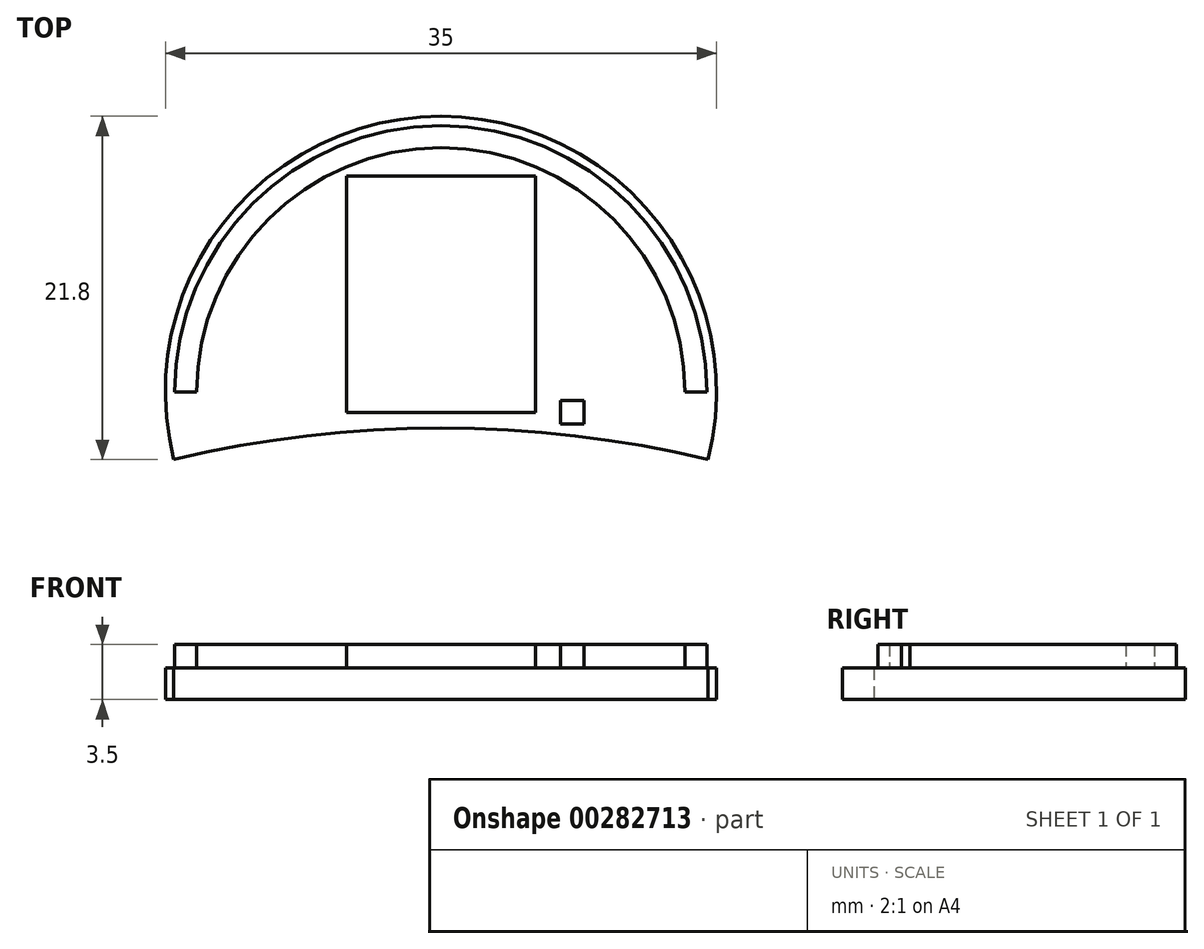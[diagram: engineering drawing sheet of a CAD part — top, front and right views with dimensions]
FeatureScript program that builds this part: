
annotation { "Feature Type Name" : "Feature", "Feature Type Description" : "" }
export const myFeature = defineFeature(function(context is Context, id is Id, definition is map)
    precondition{}
    {
        {
            var Q0;
            Q0=qCreatedBy(makeId("Top.planeOp"),FACE);
            var sketch = newSketch(context, id + "F0", { "sketchPlane" : qUnion([Q0])});
            skCircle(sketch, "E0", {"center": v(0, 0) * mm, "radius": 17.5 * mm});
            skArc(sketch, "E1", {"start": v(16.96, -4.3) * mm, "mid": v(0, -2.3) * mm, "end": v(-16.96, -4.3) * mm});
            skLineSegment(sketch, "E2", {"start": v(16.96, -4.3) * mm, "end": v(-16.96, -4.3) * mm, "construction": true});
            skLineSegment(sketch, "E3", {"start": v(0, -2.3) * mm, "end": v(0, -4.3) * mm, "construction": true});
            skLineSegment(sketch, "E4", {"start": v(0, 17.5) * mm, "end": v(18.97, 17.5) * mm, "construction": true});
            skSolve(sketch);
        }
        {
            var Q0;
            {var subQ0=sQuery(id+"F0.wireOp",EDGE,"E1");Q0=makeQuery(id+"F0.imprint","IMPRINT",FACE,{"disambiguationData":[TD([[makeQuery(id+"F0.imprint","IMPRINT",EDGE,{"derivedFrom":subQ0}),-1.0]])]});}
            extrude(context, id + "F1", {"entities" : qUnion([Q0]), "depth" : 2 * mm});
        }
        {
            var Q0;
            Q0=makeQuery(id+"F1.opExtrude","CAP_FACE",FACE,{"disambiguationData":[OSD([sQuery(id+"F0.wireOp",EDGE,"E0"),sQuery(id+"F0.wireOp",EDGE,"E1")])],"isStart":false});
            var sketch = newSketch(context, id + "F2", { "sketchPlane" : qUnion([Q0])});
            skLineSegment(sketch, "E5.bottom", {"start": v(-6, 13.7) * mm, "end": v(6, 13.7) * mm});
            skLineSegment(sketch, "E5.top", {"start": v(-6, -1.3) * mm, "end": v(6, -1.3) * mm});
            skLineSegment(sketch, "E5.left", {"start": v(-6, 13.7) * mm, "end": v(-6, -1.3) * mm});
            skLineSegment(sketch, "E5.right", {"start": v(6, 13.7) * mm, "end": v(6, -1.3) * mm});
            skPoint(sketch, "E5.middle", {"position": v(0, 6.2) * mm});
            skArc(sketch, "E6.0", {"start": v(15.7, -3.98) * mm, "mid": v(0, 16.2) * mm, "end": v(-15.7, -3.98) * mm, "construction": true});
            skArc(sketch, "E7.0", {"start": v(16.38, -4.15) * mm, "mid": v(0, 16.9) * mm, "end": v(-16.38, -4.15) * mm});
            skArc(sketch, "E8.0", {"start": v(15.02, -3.8) * mm, "mid": v(0, 15.5) * mm, "end": v(-15.02, -3.8) * mm});
            skLineSegment(sketch, "E9.bottom", {"start": v(9.1, -2.05) * mm, "end": v(7.6, -2.05) * mm});
            skLineSegment(sketch, "E9.top", {"start": v(9.1, -0.55) * mm, "end": v(7.6, -0.55) * mm});
            skLineSegment(sketch, "E9.left", {"start": v(9.1, -2.05) * mm, "end": v(9.1, -0.55) * mm});
            skLineSegment(sketch, "E9.right", {"start": v(7.6, -2.05) * mm, "end": v(7.6, -0.55) * mm});
            skPoint(sketch, "E9.middle", {"position": v(8.35, -1.3) * mm});
            skLineSegment(sketch, "E10", {"start": v(-16.9, 0) * mm, "end": v(-15.5, 0) * mm});
            skLineSegment(sketch, "E11", {"start": v(15.5, 0) * mm, "end": v(17.5, 0) * mm});
            skSolve(sketch);
        }
        {
            var Q0;
            Q0 = qSketchRegion(id + "F2", true);
            extrude(context, id + "F3", {"entities" : qUnion([Q0]), "operationType" : NewBodyOperationType.ADD, "depth" : 1.5 * mm});
        }
    });
